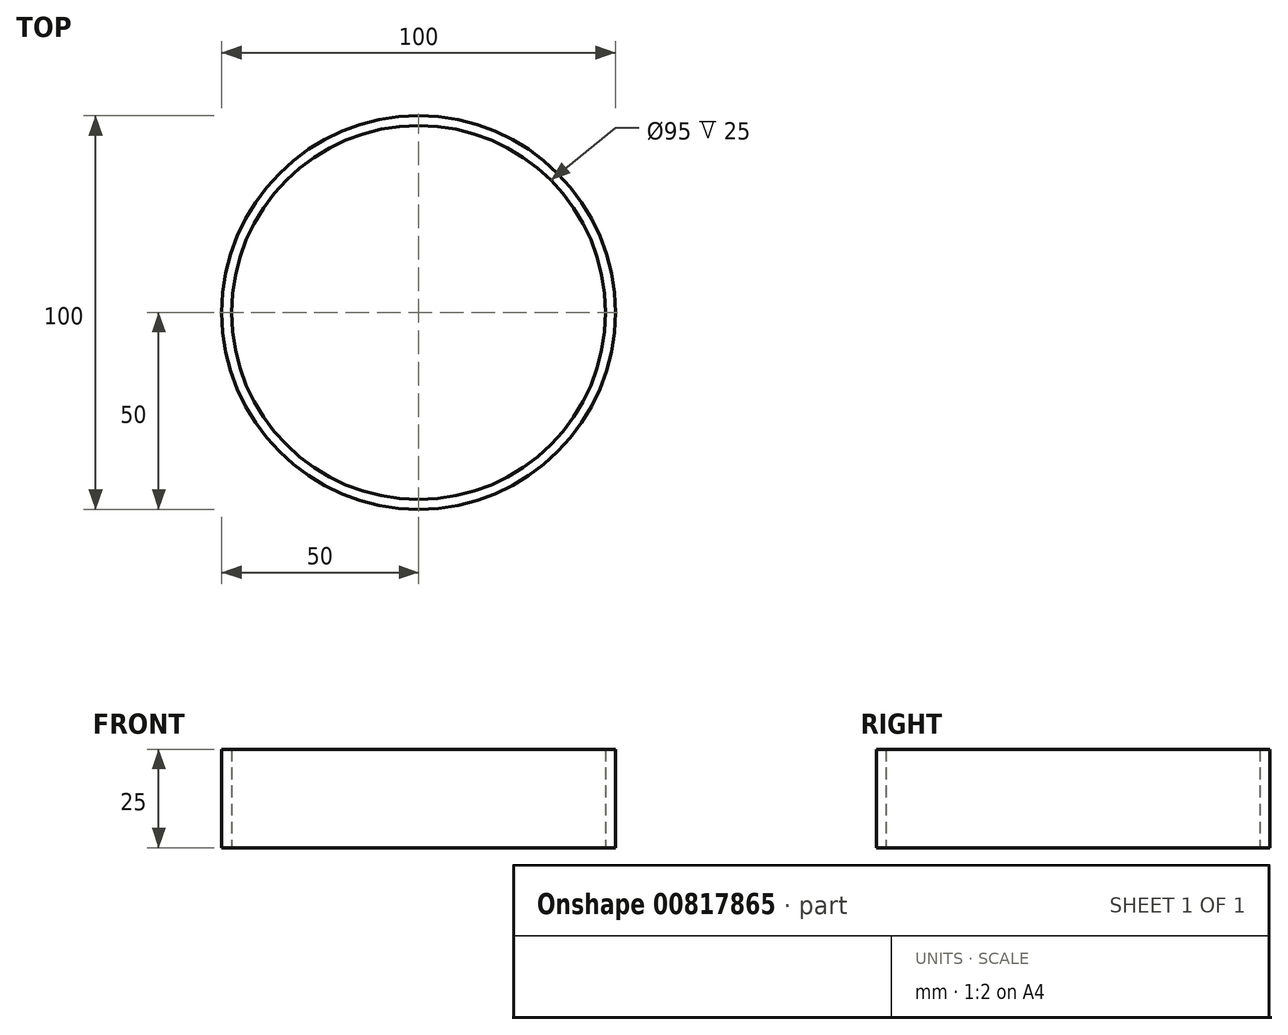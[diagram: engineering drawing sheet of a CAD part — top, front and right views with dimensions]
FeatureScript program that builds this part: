
annotation { "Feature Type Name" : "Feature", "Feature Type Description" : "" }
export const myFeature = defineFeature(function(context is Context, id is Id, definition is map)
    precondition{}
    {
        {
            var Q0;
            Q0=qCreatedBy(makeId("Top.planeOp"),FACE);
            var sketch = newSketch(context, id + "F0", { "sketchPlane" : qUnion([Q0])});
            skCircle(sketch, "E0", {"center": v(0, 0) * mm, "radius": 50 * mm});
            skCircle(sketch, "E1", {"center": v(0, 0) * mm, "radius": 47.5 * mm});
            skSolve(sketch);
        }
        {
            var Q0;
            Q0 = qSketchRegion(id + "F0", true);
            extrude(context, id + "F1", {"entities" : qUnion([Q0]), "depth" : 25 * mm, "offsetDistance" : 25 * mm});
        }
    });
